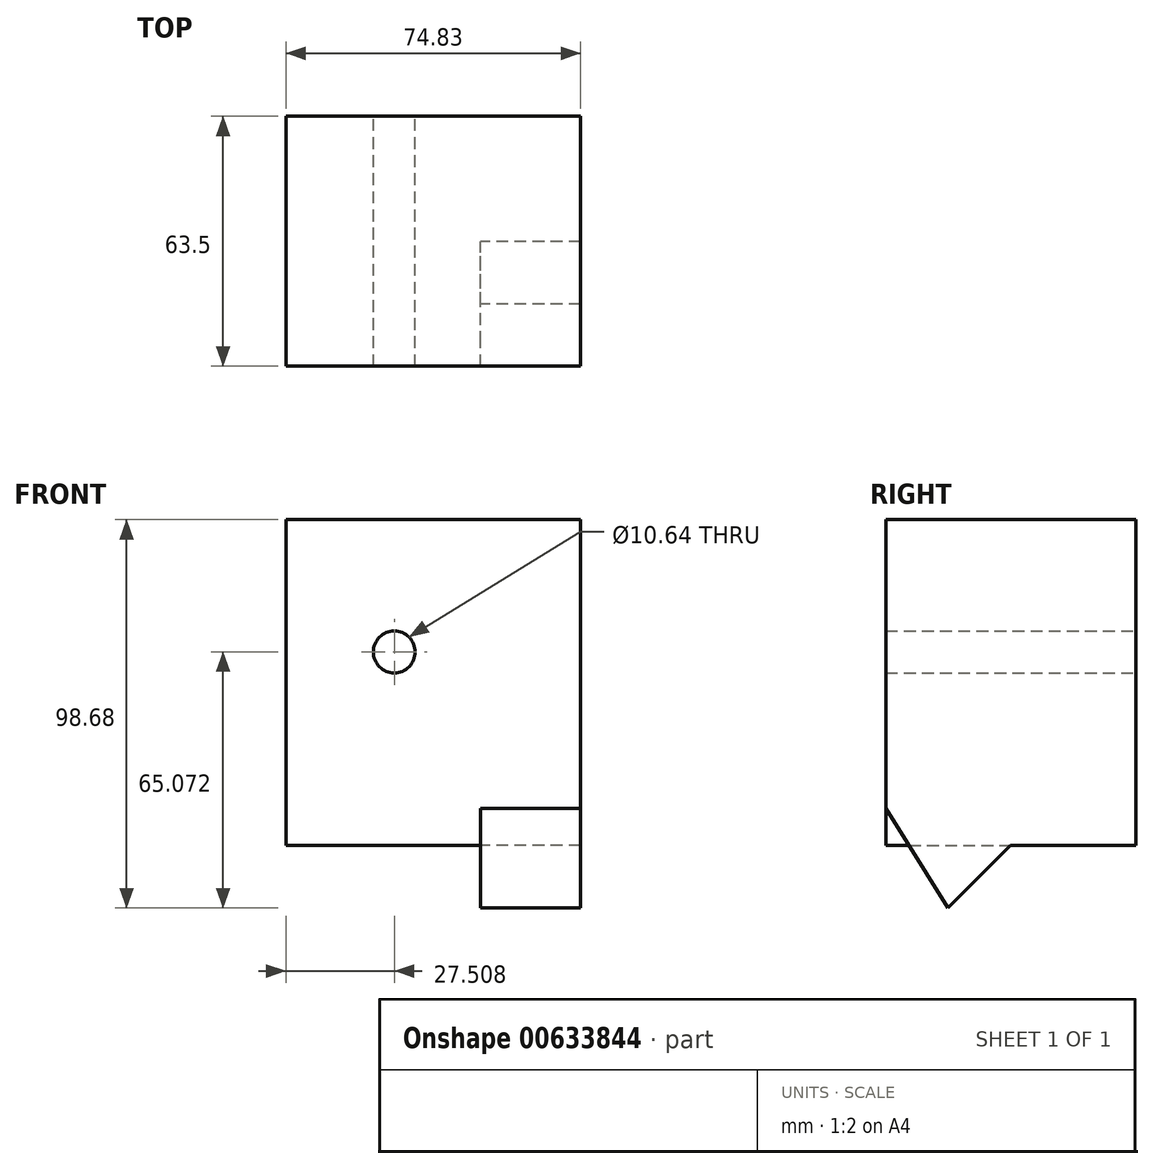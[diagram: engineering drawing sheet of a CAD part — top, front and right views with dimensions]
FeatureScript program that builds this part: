
annotation { "Feature Type Name" : "Feature", "Feature Type Description" : "" }
export const myFeature = defineFeature(function(context is Context, id is Id, definition is map)
    precondition{}
    {
        {
            var Q0;
            Q0=qCreatedBy(makeId("Front.planeOp"),FACE);
            var sketch = newSketch(context, id + "F0", { "sketchPlane" : qUnion([Q0])});
            skLineSegment(sketch, "E0.bottom", {"start": v(91.2, 35.47) * mm, "end": v(41.76, 35.47) * mm});
            skLineSegment(sketch, "E0.top", {"start": v(91.2, 118.24) * mm, "end": v(41.76, 118.24) * mm});
            skLineSegment(sketch, "E0.left", {"start": v(91.2, 35.47) * mm, "end": v(91.2, 118.24) * mm});
            skLineSegment(sketch, "E0.right", {"start": v(41.76, 35.47) * mm, "end": v(41.76, 118.24) * mm});
            skCircle(sketch, "E1", {"center": v(69.27, 84.63) * mm, "radius": 5.32 * mm});
            skSolve(sketch);
        }
        {
            var Q0;
            Q0=makeQuery(id+"F0.imprint","IMPRINT",FACE,{"disambiguationData":[TD([[makeQuery(id+"F0.imprint","IMPRINT",EDGE,{"derivedFrom":sQuery(id+"F0.wireOp",EDGE,"E0.bottom")}),-1.0]])]});
            extrude(context, id + "F1", {"entities" : qUnion([Q0]), "depth" : 63.5 * mm, "offsetDistance" : 25.4 * mm});
        }
        {
            var Q0;
            Q0=makeQuery(id+"F1.opExtrude","SWEPT_FACE",FACE,{"disambiguationData":[OSD([sQuery(id+"F0.wireOp",EDGE,"E0.left")])]});
            var sketch = newSketch(context, id + "F2", { "sketchPlane" : qUnion([Q0])});
            skPoint(sketch, "E2.2.internal.snap0", {"position": v(-63.5, 76.85) * mm});
            skFitSpline(sketch, "E2", {"points": [v(-69.89, 100.39) * mm, v(-37.65, 92.5) * mm, v(-28.27, 76.85) * mm, v(-43.14, 56.96) * mm, v(-22.12, 45.78) * mm], "startDerivative": vector(121.35, -14.5) * mm, "endDerivative": vector(131.07, -36.8) * mm});
            skLineSegment(sketch, "E3", {"start": v(-69.89, 100.39) * mm, "end": v(-69.89, 55.15) * mm});
            skLineSegment(sketch, "E4", {"start": v(-69.89, 55.15) * mm, "end": v(-47.7, 19.56) * mm});
            skLineSegment(sketch, "E5", {"start": v(-47.7, 19.56) * mm, "end": v(-20.76, 46.56) * mm});
            skSolve(sketch);
        }
        {
            var Q0;
            {var subQ0=sQuery(id+"F2.wireOp",EDGE,"E5");var subQ1=sQuery(id+"F2.wireOp",EDGE,"E4");var subQ2=makeQuery(id+"F2.imprint","INTERSECT",VERTEX,{"derivedFrom":[subQ1,subQ0]});Q0=makeQuery(id+"F2.imprint","IMPRINT",FACE,{"disambiguationData":[TD([[makeQuery(id+"F2.imprint","IMPRINT",EDGE,{"disambiguationData":[TD([[subQ2,1.0]])],"derivedFrom":subQ1}),1.0]])]});}
            var Q1;
            {var subQ0=sQuery(id+"F0.wireOp",EDGE,"E0.left");var subQ1=makeQuery(id+"F1.opExtrude","CAP_EDGE",EDGE,{"disambiguationData":[OSD([subQ0])],"isStart":true});Q1=makeQuery(id+"F2.imprint","IMPRINT",FACE,{"disambiguationData":[TD([[makeQuery(id+"F2.imprint","IMPRINT",EDGE,{"derivedFrom":subQ1}),1.0]])]});}
            extrude(context, id + "F3", {"entities" : qUnion([Q0, Q1]), "operationType" : NewBodyOperationType.ADD, "depth" : 25.4 * mm, "offsetDistance" : 25.4 * mm});
        }
    });
